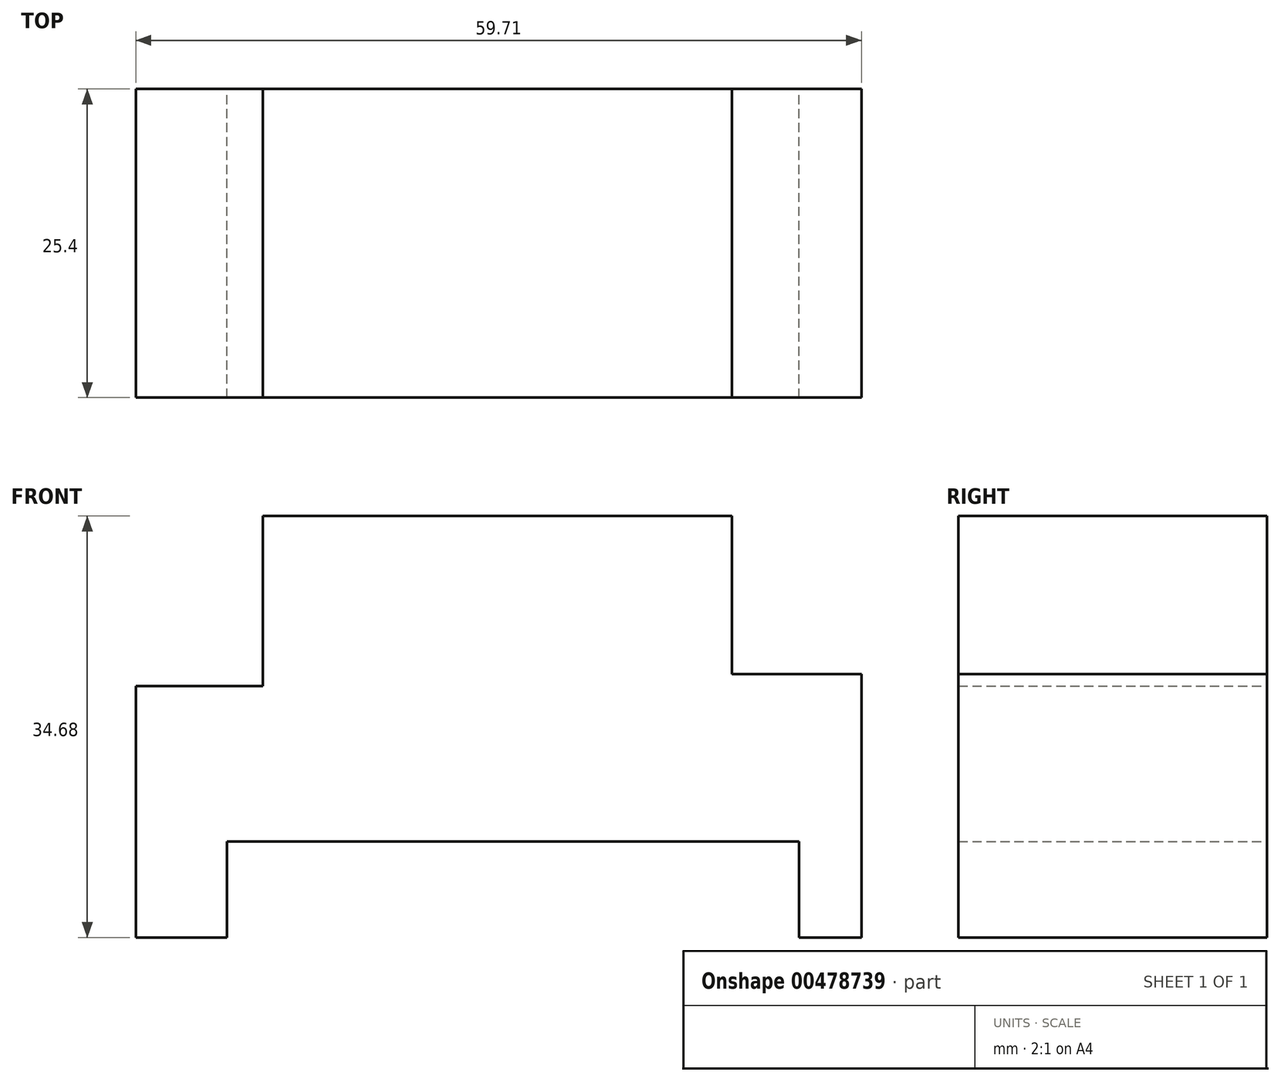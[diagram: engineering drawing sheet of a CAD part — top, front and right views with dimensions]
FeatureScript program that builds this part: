
annotation { "Feature Type Name" : "Feature", "Feature Type Description" : "" }
export const myFeature = defineFeature(function(context is Context, id is Id, definition is map)
    precondition{}
    {
        {
            var Q0;
            Q0=qCreatedBy(makeId("Front.planeOp"),FACE);
            var sketch = newSketch(context, id + "F0", { "sketchPlane" : qUnion([Q0])});
            skLineSegment(sketch, "E0", {"start": v(0, 0) * mm, "end": v(0, 20.7) * mm});
            skLineSegment(sketch, "E1", {"start": v(0, 20.7) * mm, "end": v(10.44, 20.7) * mm});
            skLineSegment(sketch, "E2", {"start": v(10.44, 20.7) * mm, "end": v(10.44, 34.68) * mm});
            skLineSegment(sketch, "E3", {"start": v(10.44, 34.68) * mm, "end": v(49.07, 34.68) * mm});
            skLineSegment(sketch, "E4", {"start": v(49.07, 34.68) * mm, "end": v(49.07, 21.68) * mm});
            skLineSegment(sketch, "E5", {"start": v(49.07, 21.68) * mm, "end": v(59.71, 21.68) * mm});
            skLineSegment(sketch, "E6", {"start": v(59.71, 21.68) * mm, "end": v(59.71, 0) * mm});
            skLineSegment(sketch, "E7", {"start": v(59.71, 0) * mm, "end": v(54.59, 0) * mm});
            skLineSegment(sketch, "E8", {"start": v(54.59, 0) * mm, "end": v(54.59, 7.88) * mm});
            skLineSegment(sketch, "E9", {"start": v(54.59, 7.88) * mm, "end": v(7.49, 7.88) * mm});
            skLineSegment(sketch, "E10", {"start": v(7.49, 7.88) * mm, "end": v(7.49, 0) * mm});
            skLineSegment(sketch, "E11", {"start": v(7.49, 0) * mm, "end": v(0, 0) * mm});
            skSolve(sketch);
        }
        {
            var Q0;
            Q0=makeQuery(id+"F0.imprint","IMPRINT",FACE,{"disambiguationData":[TD([[makeQuery(id+"F0.imprint","IMPRINT",EDGE,{"derivedFrom":sQuery(id+"F0.wireOp",EDGE,"E0")}),-1.0]])]});
            extrude(context, id + "F1", {"entities" : qUnion([Q0]), "depth" : 25.4 * mm});
        }
    });
